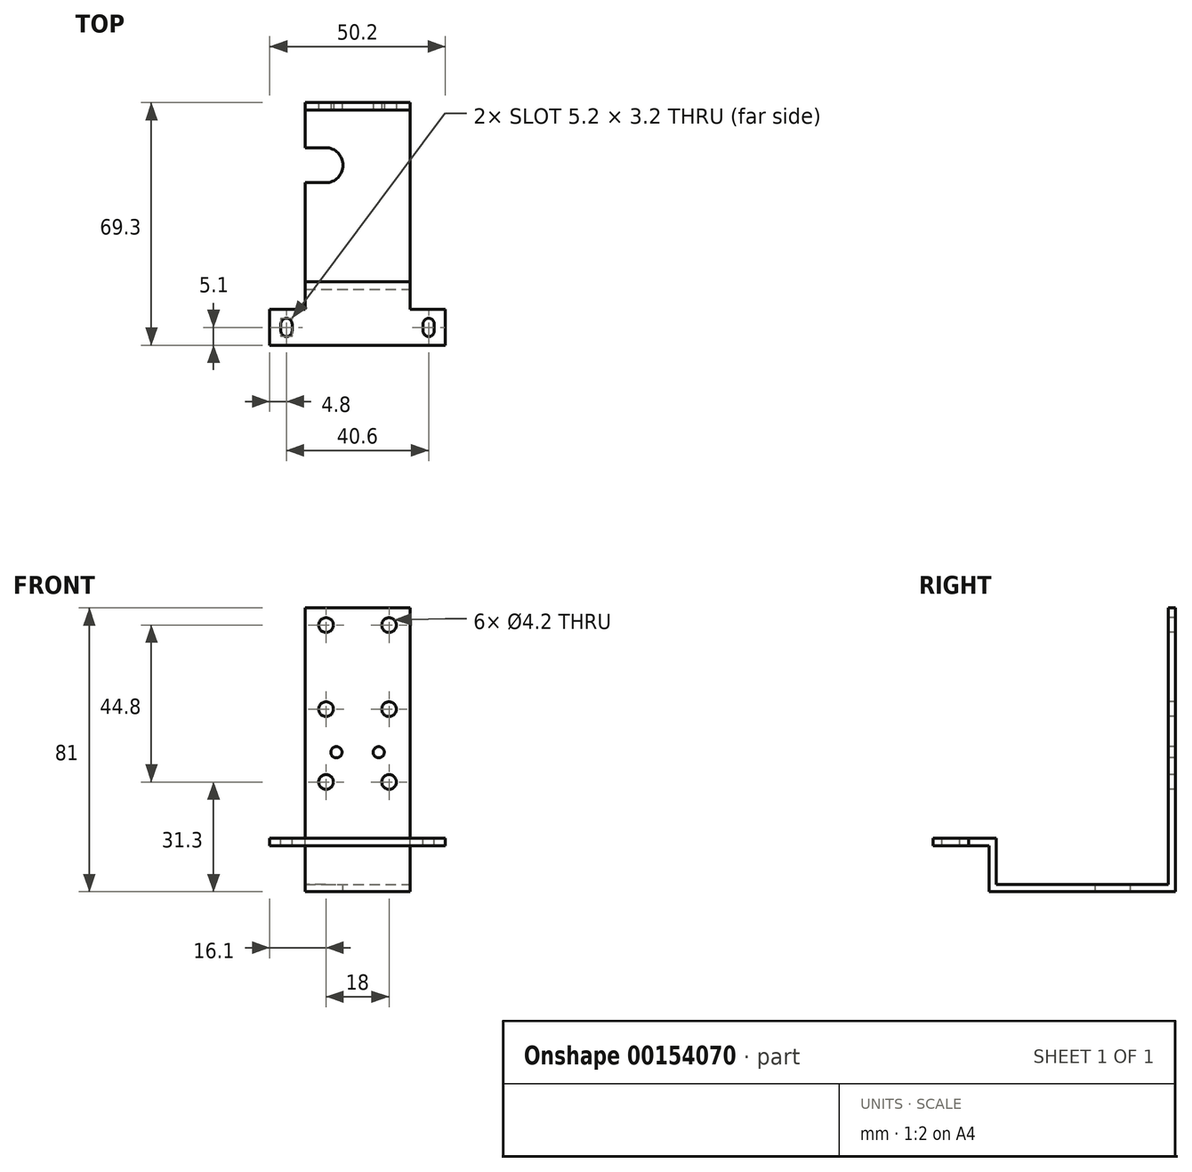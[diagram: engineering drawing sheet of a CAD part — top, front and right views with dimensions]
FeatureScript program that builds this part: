
annotation { "Feature Type Name" : "Feature", "Feature Type Description" : "" }
export const myFeature = defineFeature(function(context is Context, id is Id, definition is map)
    precondition{}
    {
        {
            var Q0;
            Q0=qCreatedBy(makeId("Front.planeOp"),FACE);
            var sketch = newSketch(context, id + "F0", { "sketchPlane" : qUnion([Q0])});
            skLineSegment(sketch, "E0.bottom", {"start": v(15, -40.5) * mm, "end": v(-15, -40.5) * mm});
            skLineSegment(sketch, "E0.top", {"start": v(15, 40.5) * mm, "end": v(-15, 40.5) * mm});
            skLineSegment(sketch, "E0.left", {"start": v(15, -40.5) * mm, "end": v(15, 40.5) * mm});
            skLineSegment(sketch, "E0.right", {"start": v(-15, -40.5) * mm, "end": v(-15, 40.5) * mm});
            skPoint(sketch, "E0.middle", {"position": v(0, 0) * mm});
            skSolve(sketch);
        }
        {
            var Q0;
            Q0 = qSketchRegion(id + "F0", true);
            extrude(context, id + "F1", {"entities" : qUnion([Q0]), "depth" : 2.1 * mm});
        }
        {
            var Q0;
            Q0=makeQuery(id+"F1.opExtrude","CAP_FACE",FACE,{"disambiguationData":[OSD([sQuery(id+"F0.wireOp",EDGE,"E0.bottom"),sQuery(id+"F0.wireOp",EDGE,"E0.top"),sQuery(id+"F0.wireOp",EDGE,"E0.left"),sQuery(id+"F0.wireOp",EDGE,"E0.right")])],"isStart":false});
            var sketch = newSketch(context, id + "F2", { "sketchPlane" : qUnion([Q0])});
            skLineSegment(sketch, "E1.bottom", {"start": v(-15, -40.5) * mm, "end": v(15, -40.5) * mm});
            skLineSegment(sketch, "E1.top", {"start": v(-15, -38.4) * mm, "end": v(15, -38.4) * mm});
            skLineSegment(sketch, "E1.left", {"start": v(-15, -40.5) * mm, "end": v(-15, -38.4) * mm});
            skLineSegment(sketch, "E1.right", {"start": v(15, -40.5) * mm, "end": v(15, -38.4) * mm});
            skSolve(sketch);
        }
        {
            var Q0;
            Q0 = qSketchRegion(id + "F2", true);
            extrude(context, id + "F3", {"entities" : qUnion([Q0]), "operationType" : NewBodyOperationType.ADD, "depth" : 51.2 * mm});
        }
        {
            var Q0;
            Q0=makeQuery(id+"F3.opExtrude","SWEPT_FACE",FACE,{"disambiguationData":[OSD([sQuery(id+"F2.wireOp",EDGE,"E1.top")])]});
            var sketch = newSketch(context, id + "F4", { "sketchPlane" : qUnion([Q0])});
            skLineSegment(sketch, "E2.bottom", {"start": v(-15, -53.3) * mm, "end": v(15, -53.3) * mm});
            skLineSegment(sketch, "E2.top", {"start": v(-15, -51.2) * mm, "end": v(15, -51.2) * mm});
            skLineSegment(sketch, "E2.left", {"start": v(-15, -53.3) * mm, "end": v(-15, -51.2) * mm});
            skLineSegment(sketch, "E2.right", {"start": v(15, -53.3) * mm, "end": v(15, -51.2) * mm});
            skSolve(sketch);
        }
        {
            var Q0;
            Q0 = qSketchRegion(id + "F4", true);
            extrude(context, id + "F5", {"entities" : qUnion([Q0]), "operationType" : NewBodyOperationType.ADD, "depth" : 13.1 * mm});
        }
        {
            var Q0;
            Q0=makeQuery(id+"F5.boolean.opBoolean","MERGE",FACE,{"derivedFrom":[makeQuery(id+"F3.opExtrude","CAP_FACE",FACE,{"disambiguationData":[OSD([sQuery(id+"F2.wireOp",EDGE,"E1.bottom"),sQuery(id+"F2.wireOp",EDGE,"E1.top"),sQuery(id+"F2.wireOp",EDGE,"E1.left"),sQuery(id+"F2.wireOp",EDGE,"E1.right")])],"isStart":false}),makeQuery(id+"F5.opExtrude","SWEPT_FACE",FACE,{"disambiguationData":[OSD([sQuery(id+"F4.wireOp",EDGE,"E2.bottom")])]})]});
            var sketch = newSketch(context, id + "F6", { "sketchPlane" : qUnion([Q0])});
            skLineSegment(sketch, "E3.bottom", {"start": v(-15, -25.3) * mm, "end": v(15, -25.3) * mm});
            skLineSegment(sketch, "E3.top", {"start": v(-15, -27.4) * mm, "end": v(15, -27.4) * mm});
            skLineSegment(sketch, "E3.left", {"start": v(-15, -25.3) * mm, "end": v(-15, -27.4) * mm});
            skLineSegment(sketch, "E3.right", {"start": v(15, -25.3) * mm, "end": v(15, -27.4) * mm});
            skSolve(sketch);
        }
        {
            var Q0;
            Q0 = qSketchRegion(id + "F6", true);
            extrude(context, id + "F7", {"entities" : qUnion([Q0]), "operationType" : NewBodyOperationType.ADD, "depth" : 16 * mm});
        }
        {
            var Q0;
            Q0=makeQuery(id+"F7.boolean.opBoolean","MERGE",FACE,{"derivedFrom":[makeQuery(id+"F5.opExtrude","CAP_FACE",FACE,{"disambiguationData":[OSD([sQuery(id+"F4.wireOp",EDGE,"E2.bottom"),sQuery(id+"F4.wireOp",EDGE,"E2.top"),sQuery(id+"F4.wireOp",EDGE,"E2.left"),sQuery(id+"F4.wireOp",EDGE,"E2.right")])],"isStart":false}),makeQuery(id+"F7.opExtrude","SWEPT_FACE",FACE,{"disambiguationData":[OSD([sQuery(id+"F6.wireOp",EDGE,"E3.bottom")])]})]});
            var sketch = newSketch(context, id + "F8", { "sketchPlane" : qUnion([Q0])});
            skLineSegment(sketch, "E4.bottom", {"start": v(-25.1, -69.3) * mm, "end": v(25.1, -69.3) * mm});
            skLineSegment(sketch, "E4.top", {"start": v(-25.1, -59.1) * mm, "end": v(25.1, -59.1) * mm});
            skLineSegment(sketch, "E4.left", {"start": v(-25.1, -69.3) * mm, "end": v(-25.1, -59.1) * mm});
            skLineSegment(sketch, "E4.right", {"start": v(25.1, -69.3) * mm, "end": v(25.1, -59.1) * mm});
            skLineSegment(sketch, "E5", {"start": v(0, -51.2) * mm, "end": v(0, -65.26) * mm});
            skSolve(sketch);
        }
        {
            var Q0;
            {var subQ3=sQuery(id+"F8.wireOp",EDGE,"E4.left");Q0=makeQuery(id+"F8.imprint","IMPRINT",FACE,{"disambiguationData":[TD([[makeQuery(id+"F8.imprint","IMPRINT",EDGE,{"derivedFrom":subQ3}),-1.0]])]});}
            var Q1;
            {var subQ3=sQuery(id+"F8.wireOp",EDGE,"E4.right");Q1=makeQuery(id+"F8.imprint","IMPRINT",FACE,{"disambiguationData":[TD([[makeQuery(id+"F8.imprint","IMPRINT",EDGE,{"derivedFrom":subQ3}),1.0]])]});}
            extrude(context, id + "F9", {"entities" : qUnion([Q0, Q1]), "operationType" : NewBodyOperationType.ADD, "oppositeDirection" : true, "depth" : 2.1 * mm});
        }
        {
            var Q0;
            {var subQ0=sQuery(id+"F8.wireOp",EDGE,"E4.top");var subQ1=sQuery(id+"F8.wireOp",EDGE,"E4.bottom");var subQ2=sQuery(id+"F6.wireOp",EDGE,"E3.bottom");var subQ3=sQuery(id+"F4.wireOp",EDGE,"E2.right");var subQ4=sQuery(id+"F4.wireOp",EDGE,"E2.left");Q0=makeQuery(id+"F9.boolean.opBoolean","MERGE",FACE,{"derivedFrom":[makeQuery(id+"F7.boolean.opBoolean","MERGE",FACE,{"derivedFrom":[makeQuery(id+"F5.opExtrude","CAP_FACE",FACE,{"disambiguationData":[OSD([sQuery(id+"F4.wireOp",EDGE,"E2.bottom"),sQuery(id+"F4.wireOp",EDGE,"E2.top"),subQ4,subQ3])],"isStart":false}),makeQuery(id+"F7.opExtrude","SWEPT_FACE",FACE,{"disambiguationData":[OSD([subQ2])]})]}),makeQuery(id+"F9.opExtrude","CAP_FACE",FACE,{"disambiguationData":[OSD([subQ4,subQ2,sQuery(id+"F6.wireOp",EDGE,"E3.left"),subQ1,subQ0,sQuery(id+"F8.wireOp",EDGE,"E4.left")])],"isStart":true}),makeQuery(id+"F9.opExtrude","CAP_FACE",FACE,{"disambiguationData":[OSD([subQ3,subQ2,sQuery(id+"F6.wireOp",EDGE,"E3.right"),subQ1,subQ0,sQuery(id+"F8.wireOp",EDGE,"E4.right")])],"isStart":true})]});}
            var sketch = newSketch(context, id + "F10", { "sketchPlane" : qUnion([Q0])});
            skArc(sketch, "E6", {"start": v(-21.9, -65.2) * mm, "mid": v(-20.3, -66.8) * mm, "end": v(-18.7, -65.2) * mm});
            skArc(sketch, "E7", {"start": v(-18.7, -63.2) * mm, "mid": v(-20.3, -61.6) * mm, "end": v(-21.9, -63.2) * mm});
            skLineSegment(sketch, "E8", {"start": v(-21.9, -63.2) * mm, "end": v(-21.9, -65.2) * mm});
            skLineSegment(sketch, "E9", {"start": v(-18.7, -65.2) * mm, "end": v(-18.7, -63.2) * mm});
            skLineSegment(sketch, "E10", {"start": v(-20.3, -63.2) * mm, "end": v(-20.3, -65.2) * mm});
            skPoint(sketch, "E11", {"position": v(-20.3, -64.2) * mm});
            skLineSegment(sketch, "E12", {"start": v(0, -69.3) * mm, "end": v(0, -51.2) * mm});
            skLineSegment(sketch, "E13.MirrorCS", {"start": v(18.7, -65.2) * mm, "end": v(18.7, -63.2) * mm});
            skArc(sketch, "E14.MirrorCS", {"start": v(18.7, -63.2) * mm, "mid": v(20.3, -61.6) * mm, "end": v(21.9, -63.2) * mm});
            skLineSegment(sketch, "E15.MirrorCS", {"start": v(21.9, -63.2) * mm, "end": v(21.9, -65.2) * mm});
            skArc(sketch, "E16.MirrorCS", {"start": v(21.9, -65.2) * mm, "mid": v(20.3, -66.8) * mm, "end": v(18.7, -65.2) * mm});
            skSolve(sketch);
        }
        {
            var Q0;
            Q0=makeQuery(id+"F10.imprint","IMPRINT",FACE,{"disambiguationData":[TD([[makeQuery(id+"F10.imprint","IMPRINT",EDGE,{"derivedFrom":sQuery(id+"F10.wireOp",EDGE,"E6")}),1.0]])]});
            var Q1;
            Q1=makeQuery(id+"F10.imprint","IMPRINT",FACE,{"disambiguationData":[TD([[makeQuery(id+"F10.imprint","IMPRINT",EDGE,{"derivedFrom":sQuery(id+"F10.wireOp",EDGE,"E13.MirrorCS")}),-1.0]])]});
            extrude(context, id + "F11", {"entities" : qUnion([Q0, Q1]), "operationType" : NewBodyOperationType.REMOVE, "endBound" : BoundingType.THROUGH_ALL, "oppositeDirection" : true, "depth" : 25 * mm});
        }
        {
            var Q0;
            Q0=makeQuery(id+"F3.opExtrude","SWEPT_FACE",FACE,{"disambiguationData":[OSD([sQuery(id+"F2.wireOp",EDGE,"E1.top")])]});
            var sketch = newSketch(context, id + "F12", { "sketchPlane" : qUnion([Q0])});
            skArc(sketch, "E17", {"start": v(-9.15, -22.9) * mm, "mid": v(-4.15, -17.9) * mm, "end": v(-9.15, -12.9) * mm});
            skLineSegment(sketch, "E18", {"start": v(-9.15, -12.9) * mm, "end": v(-15, -12.9) * mm});
            skLineSegment(sketch, "E19", {"start": v(-9.15, -22.9) * mm, "end": v(-15, -22.9) * mm});
            skLineSegment(sketch, "E20", {"start": v(-15, -22.9) * mm, "end": v(-15, -12.9) * mm});
            skSolve(sketch);
        }
        {
            var Q0;
            Q0 = qSketchRegion(id + "F12", true);
            extrude(context, id + "F13", {"entities" : qUnion([Q0]), "operationType" : NewBodyOperationType.REMOVE, "endBound" : BoundingType.THROUGH_ALL, "oppositeDirection" : true, "depth" : 25 * mm});
        }
        {
            var Q0;
            Q0=makeQuery(id+"F1.opExtrude","CAP_FACE",FACE,{"disambiguationData":[OSD([sQuery(id+"F0.wireOp",EDGE,"E0.bottom"),sQuery(id+"F0.wireOp",EDGE,"E0.top"),sQuery(id+"F0.wireOp",EDGE,"E0.left"),sQuery(id+"F0.wireOp",EDGE,"E0.right")])],"isStart":false});
            var sketch = newSketch(context, id + "F14", { "sketchPlane" : qUnion([Q0])});
            skCircle(sketch, "E21", {"center": v(9, 35.6) * mm, "radius": 2.1 * mm});
            skCircle(sketch, "E22.0.1.0", {"center": v(9, 11.6) * mm, "radius": 2.1 * mm});
            skCircle(sketch, "E22.1.0.0", {"center": v(-9, 35.6) * mm, "radius": 2.1 * mm});
            skCircle(sketch, "E22.1.1.0", {"center": v(-9, 11.6) * mm, "radius": 2.1 * mm});
            skLineSegment(sketch, "E22.direction1", {"start": v(9, 35.6) * mm, "end": v(-9, 35.6) * mm, "construction": true});
            skLineSegment(sketch, "E22.direction2", {"start": v(9, 35.6) * mm, "end": v(9, 11.6) * mm, "construction": true});
            skCircle(sketch, "E23", {"center": v(9, -9.2) * mm, "radius": 2.1 * mm});
            skCircle(sketch, "E24.1.0.0", {"center": v(-9, -9.2) * mm, "radius": 2.1 * mm});
            skLineSegment(sketch, "E24.direction1", {"start": v(9, -9.2) * mm, "end": v(-9, -9.2) * mm, "construction": true});
            skCircle(sketch, "E25", {"center": v(6.05, -0.7) * mm, "radius": 1.6 * mm});
            skCircle(sketch, "E26", {"center": v(-6.05, -0.7) * mm, "radius": 1.6 * mm});
            skSolve(sketch);
        }
        {
            var Q0;
            Q0 = qSketchRegion(id + "F14", true);
            extrude(context, id + "F15", {"entities" : qUnion([Q0]), "operationType" : NewBodyOperationType.REMOVE, "endBound" : BoundingType.THROUGH_ALL, "oppositeDirection" : true, "depth" : 25 * mm});
        }
    });
